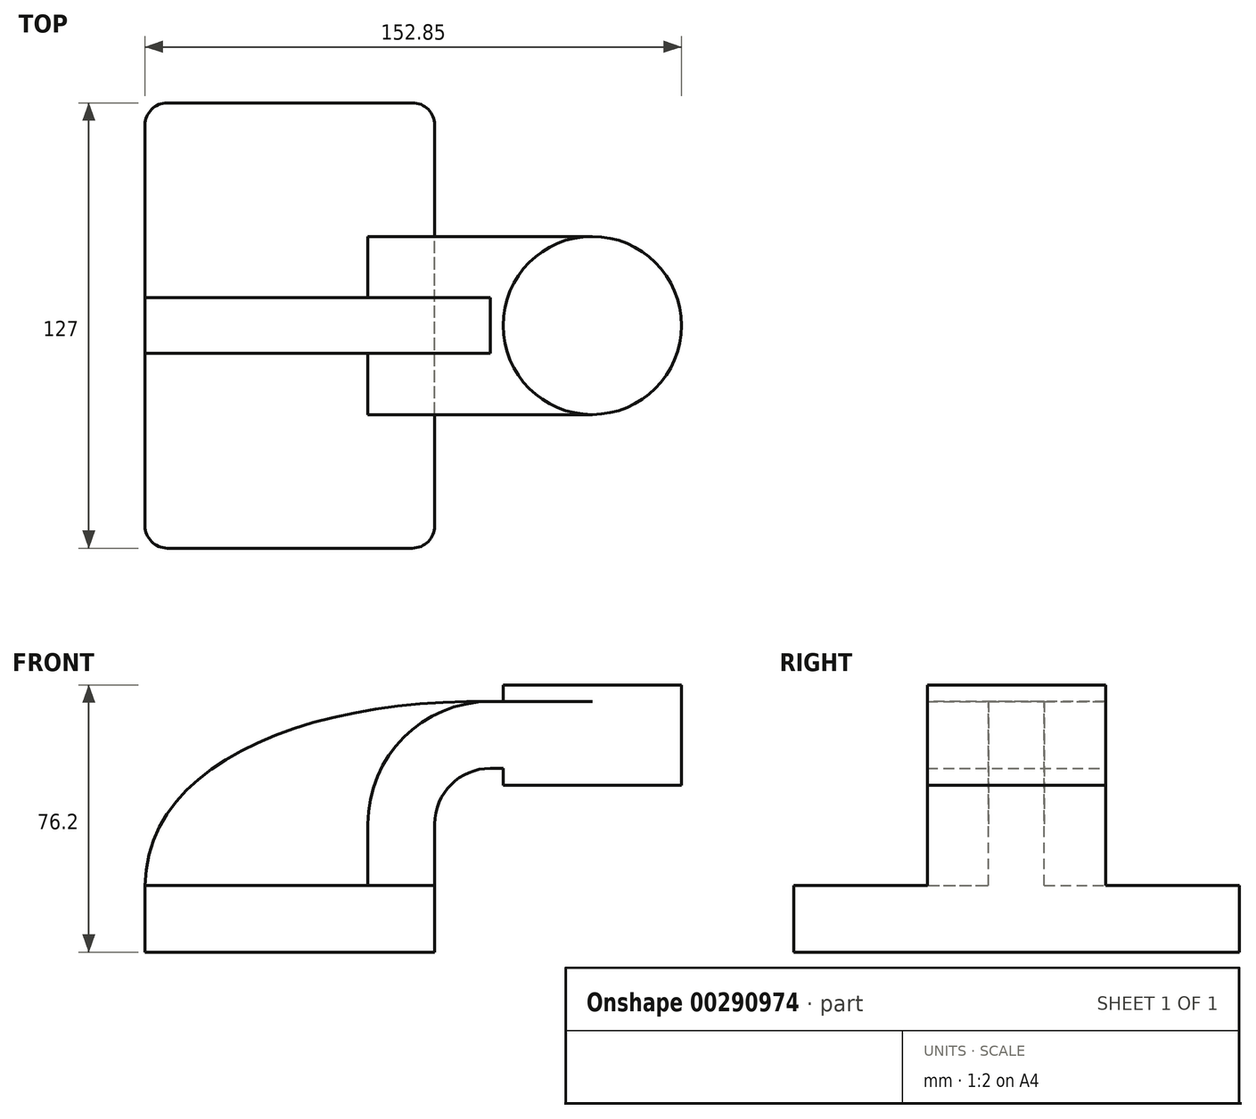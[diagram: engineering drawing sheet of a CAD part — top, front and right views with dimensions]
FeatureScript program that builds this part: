
annotation { "Feature Type Name" : "Feature", "Feature Type Description" : "" }
export const myFeature = defineFeature(function(context is Context, id is Id, definition is map)
    precondition{}
    {
        {
            var Q0;
            Q0=qCreatedBy(makeId("Front.planeOp"),FACE);
            var sketch = newSketch(context, id + "F0", { "sketchPlane" : qUnion([Q0])});
            skLineSegment(sketch, "E0.bottom", {"start": v(-46.1, 15.04) * mm, "end": v(36.46, 15.04) * mm});
            skLineSegment(sketch, "E0.top", {"start": v(-46.1, 34.1) * mm, "end": v(36.46, 34.1) * mm});
            skLineSegment(sketch, "E0.left", {"start": v(-46.1, 15.04) * mm, "end": v(-46.1, 34.1) * mm});
            skLineSegment(sketch, "E0.right", {"start": v(36.46, 15.04) * mm, "end": v(36.46, 34.1) * mm});
            skLineSegment(sketch, "E1.bottom", {"start": v(55.96, 91.24) * mm, "end": v(106.76, 91.24) * mm});
            skLineSegment(sketch, "E1.top", {"start": v(55.96, 62.67) * mm, "end": v(106.76, 62.67) * mm});
            skLineSegment(sketch, "E1.left", {"start": v(55.96, 91.24) * mm, "end": v(55.96, 62.67) * mm});
            skLineSegment(sketch, "E1.right", {"start": v(106.76, 91.24) * mm, "end": v(106.76, 62.67) * mm});
            skLineSegment(sketch, "E2", {"start": v(36.46, 34.1) * mm, "end": v(36.46, 51.57) * mm});
            skLineSegment(sketch, "E3", {"start": v(52.33, 67.44) * mm, "end": v(65.8, 67.44) * mm});
            skArc(sketch, "E4", {"start": v(52.33, 67.44) * mm, "mid": v(41.1, 62.8) * mm, "end": v(36.46, 51.57) * mm});
            skLineSegment(sketch, "E5.0", {"start": v(52.33, 86.5) * mm, "end": v(81.36, 86.5) * mm});
            skArc(sketch, "E5.1", {"start": v(52.33, 86.5) * mm, "mid": v(27.64, 76.26) * mm, "end": v(17.4, 51.57) * mm});
            skLineSegment(sketch, "E5.2", {"start": v(17.4, 34.1) * mm, "end": v(17.4, 51.57) * mm});
            skLineSegment(sketch, "E6", {"start": v(81.36, 91.24) * mm, "end": v(81.36, 62.67) * mm});
            skFitSpline(sketch, "E7", {"points": [v(-46.1, 34.1) * mm, v(52.33, 86.5) * mm], "startDerivative": vector(0.74, 103.94) * mm, "endDerivative": vector(157, -2.56) * mm});
            skSolve(sketch);
        }
        {
            var Q0;
            Q0=makeQuery(id+"F0.imprint","IMPRINT",FACE,{"disambiguationData":[TD([[makeQuery(id+"F0.imprint","IMPRINT",EDGE,{"derivedFrom":sQuery(id+"F0.wireOp",EDGE,"E0.bottom")}),1.0]])]});
            extrude(context, id + "F1", {"entities" : qUnion([Q0]), "endBound" : BoundingType.SYMMETRIC, "depth" : 127 * mm});
        }
        {
            var Q0;
            {var subQ4=sQuery(id+"F0.wireOp",EDGE,"E2");Q0=makeQuery(id+"F0.imprint","IMPRINT",FACE,{"disambiguationData":[TD([[makeQuery(id+"F0.imprint","IMPRINT",EDGE,{"derivedFrom":subQ4}),1.0]])]});}
            var Q1;
            {var subQ0=sQuery(id+"F0.wireOp",EDGE,"E5.0");var subQ1=sQuery(id+"F0.wireOp",EDGE,"E1.left");var subQ2=makeQuery(id+"F0.imprint","INTERSECT",VERTEX,{"derivedFrom":[subQ1,subQ0]});Q1=makeQuery(id+"F0.imprint","IMPRINT",FACE,{"disambiguationData":[TD([[makeQuery(id+"F0.imprint","IMPRINT",EDGE,{"disambiguationData":[TD([[subQ2,-1.0]])],"derivedFrom":subQ1}),1.0]])]});}
            extrude(context, id + "F2", {"entities" : qUnion([Q0, Q1]), "operationType" : NewBodyOperationType.ADD, "endBound" : BoundingType.SYMMETRIC, "depth" : 50.8 * mm});
        }
        {
            var Q0;
            Q0=makeQuery(id+"F0.imprint","IMPRINT",FACE,{"disambiguationData":[TD([[makeQuery(id+"F0.imprint","IMPRINT",EDGE,{"derivedFrom":sQuery(id+"F0.wireOp",EDGE,"E5.1")}),-1.0]])]});
            extrude(context, id + "F3", {"entities" : qUnion([Q0]), "operationType" : NewBodyOperationType.ADD, "endBound" : BoundingType.SYMMETRIC, "depth" : 15.88 * mm});
        }
        {
            var Q0;
            {var subQ4=sQuery(id+"F0.wireOp",EDGE,"E1.right");Q0=makeQuery(id+"F0.imprint","IMPRINT",FACE,{"disambiguationData":[TD([[makeQuery(id+"F0.imprint","IMPRINT",EDGE,{"derivedFrom":subQ4}),-1.0]])]});}
            var Q1;
            Q1=sQuery(id+"F0.wireOp",EDGE,"E6");
            revolve(context, id + "F4", {"operationType" : NewBodyOperationType.ADD, "entities" : qUnion([Q0]), "axis" : qUnion([Q1]), "revolveType" : RevolveType.FULL});
        }
        {
            var Q0;
            Q0=makeQuery(id+"F1.opExtrude","CAP_EDGE",EDGE,{"disambiguationData":[OSD([sQuery(id+"F0.wireOp",EDGE,"E0.right")])],"isStart":false});
            var Q1;
            Q1=makeQuery(id+"F1.opExtrude","CAP_EDGE",EDGE,{"disambiguationData":[OSD([sQuery(id+"F0.wireOp",EDGE,"E0.left")])],"isStart":false});
            var Q2;
            Q2=makeQuery(id+"F1.opExtrude","CAP_EDGE",EDGE,{"disambiguationData":[OSD([sQuery(id+"F0.wireOp",EDGE,"E0.right")])],"isStart":true});
            var Q3;
            Q3=makeQuery(id+"F1.opExtrude","CAP_EDGE",EDGE,{"disambiguationData":[OSD([sQuery(id+"F0.wireOp",EDGE,"E0.left")])],"isStart":true});
            fillet(context, id + "F5", {"entities" : qUnion([Q0, Q1, Q2, Q3]), "radius" : 6.35 * mm, "tangentPropagation" : true, "allowEdgeOverflow" : false});
        }
    });
